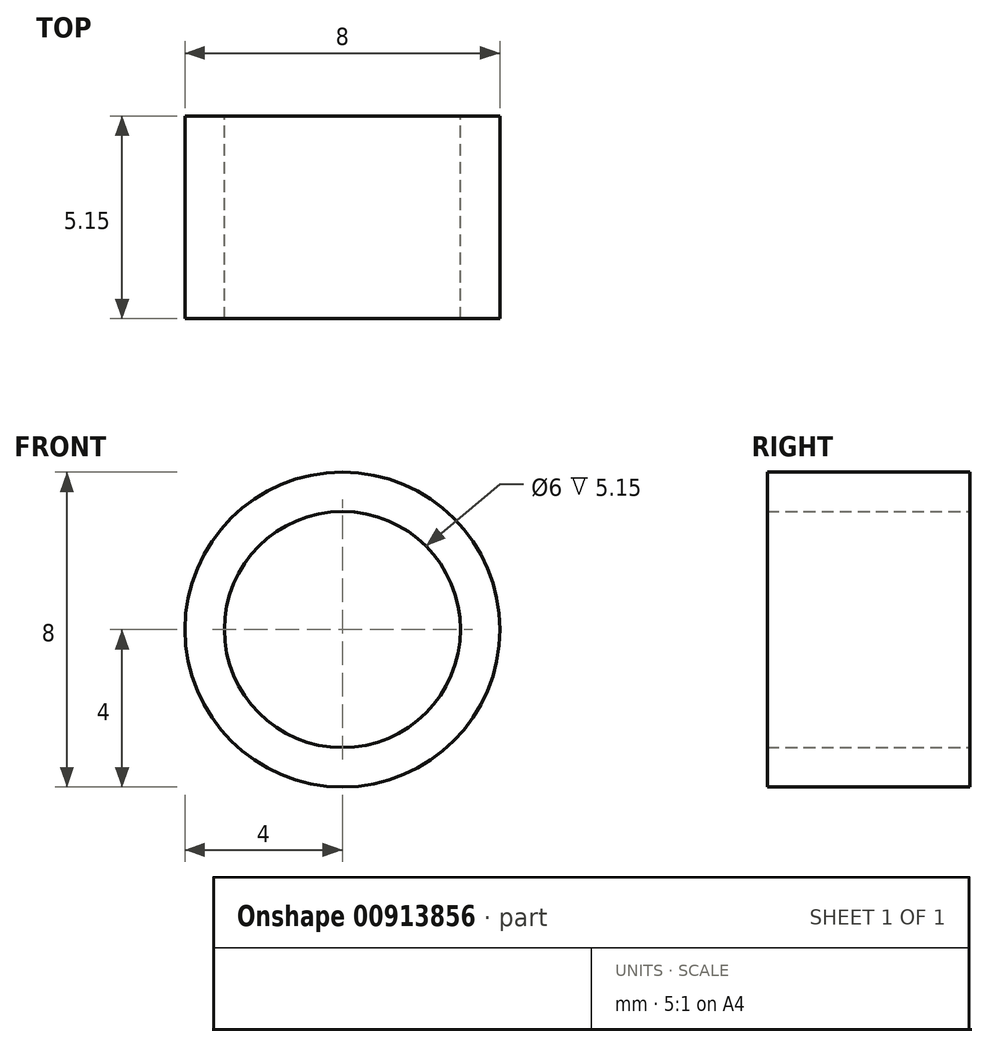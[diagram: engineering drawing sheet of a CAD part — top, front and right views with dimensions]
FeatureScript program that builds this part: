
annotation { "Feature Type Name" : "Feature", "Feature Type Description" : "" }
export const myFeature = defineFeature(function(context is Context, id is Id, definition is map)
    precondition{}
    {
        {
            var Q0;
            Q0=qCreatedBy(makeId("Front.planeOp"),FACE);
            var sketch = newSketch(context, id + "F0", { "sketchPlane" : qUnion([Q0])});
            skCircle(sketch, "E0", {"center": v(0, 0) * mm, "radius": 4 * mm});
            skCircle(sketch, "E1", {"center": v(0, 0) * mm, "radius": 3 * mm});
            skSolve(sketch);
        }
        {
            var Q0;
            Q0=qSketchRegion(id+"F0",true);
            extrude(context, id + "F1", {"entities" : qUnion([Q0]), "depth" : 5.15 * mm, "offsetDistance" : 25 * mm});
        }
    });
